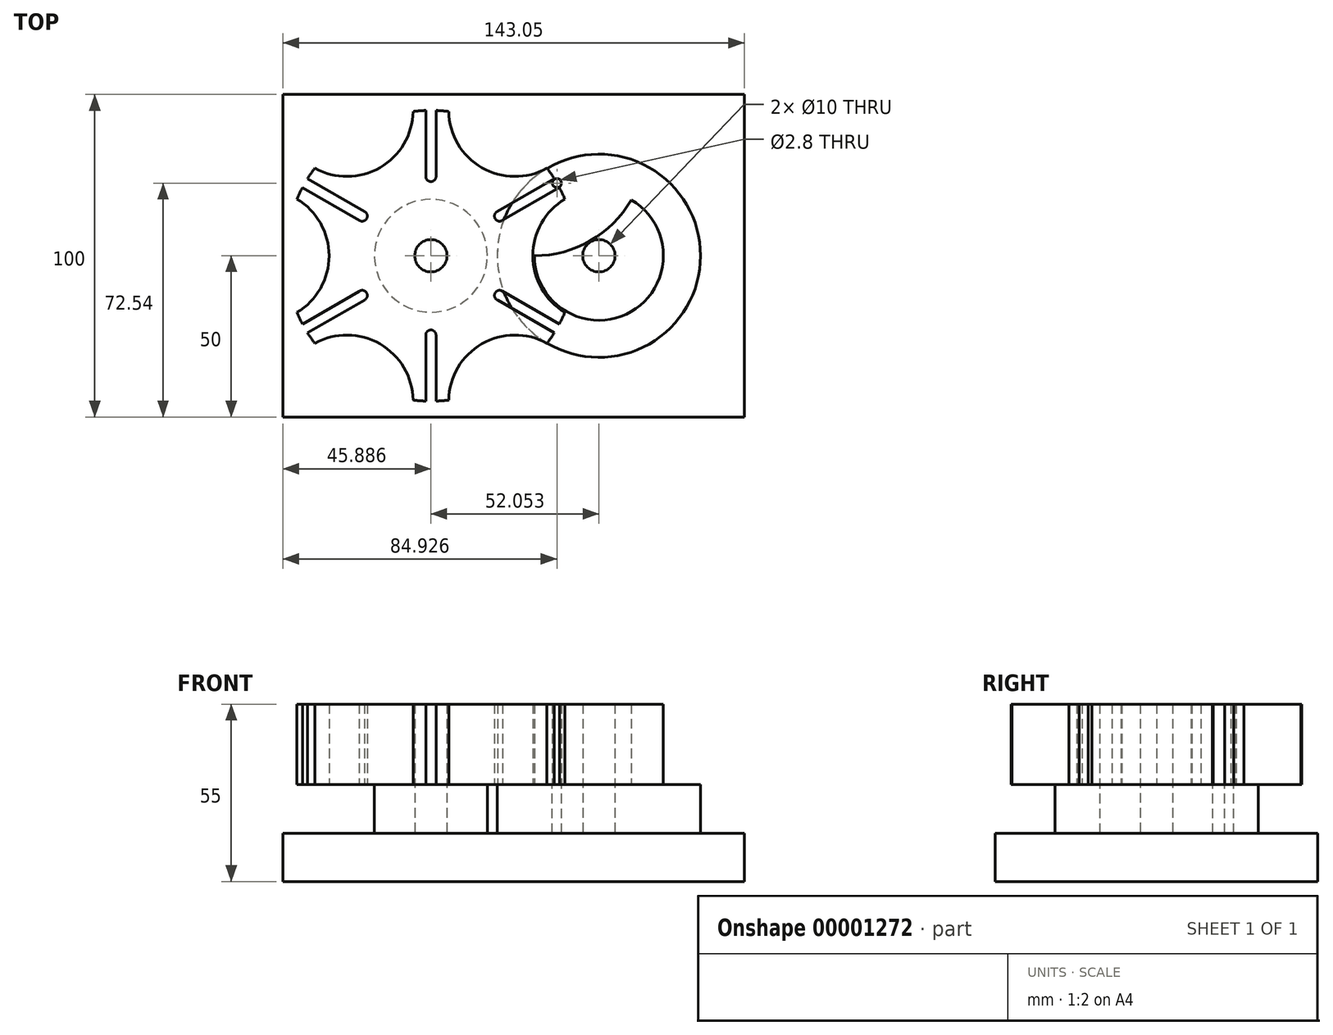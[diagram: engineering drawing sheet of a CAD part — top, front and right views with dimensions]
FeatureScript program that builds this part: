
annotation { "Feature Type Name" : "Feature", "Feature Type Description" : "" }
export const myFeature = defineFeature(function(context is Context, id is Id, definition is map)
    precondition{}
    {
        {
            var Q0;
            Q0=qCreatedBy(makeId("Top.planeOp"),FACE);
            var sketch = newSketch(context, id + "F0", { "sketchPlane" : qUnion([Q0])});
            skCircle(sketch, "E0", {"center": v(-6.18, 0) * mm, "radius": 45.08 * mm});
            skCircle(sketch, "E1", {"center": v(45.87, 0) * mm, "radius": 31.5 * mm});
            skCircle(sketch, "E2", {"center": v(45.87, 0) * mm, "radius": 20 * mm});
            skLineSegment(sketch, "E3", {"start": v(-6.18, 0) * mm, "end": v(-6.18, 45.08) * mm, "construction": true});
            skLineSegment(sketch, "E4", {"start": v(45.87, 0) * mm, "end": v(45.87, 31.5) * mm, "construction": true});
            skLineSegment(sketch, "E5", {"start": v(45.87, 20) * mm, "end": v(45.87, 31.5) * mm, "construction": true});
            skLineSegment(sketch, "E6", {"start": v(-6.18, 0) * mm, "end": v(45.87, 0) * mm, "construction": true});
            skLineSegment(sketch, "E7", {"start": v(45.87, 0) * mm, "end": v(32.86, 22.54) * mm, "construction": true});
            skLineSegment(sketch, "E8", {"start": v(32.86, 22.54) * mm, "end": v(-6.18, 0) * mm, "construction": true});
            skCircle(sketch, "E9", {"center": v(45.87, 0) * mm, "radius": 26.03 * mm, "construction": true});
            skLineSegment(sketch, "E10", {"start": v(32.86, 22.54) * mm, "end": v(15.21, 53.1) * mm, "construction": true});
            skLineSegment(sketch, "E11", {"start": v(32.86, 22.54) * mm, "end": v(15.11, 12.3) * mm});
            skArc(sketch, "E12", {"start": v(14.32, 13.67) * mm, "mid": v(13.77, 11.44) * mm, "end": v(16.03, 11) * mm});
            skLineSegment(sketch, "E13", {"start": v(16.03, 11) * mm, "end": v(33.65, 21.17) * mm});
            skLineSegment(sketch, "E14", {"start": v(32.04, 23.9) * mm, "end": v(14.32, 13.67) * mm});
            skCircle(sketch, "E15", {"center": v(32.86, 22.54) * mm, "radius": 1.4 * mm});
            skArc(sketch, "E16", {"start": v(35.62, 17.75) * mm, "mid": v(25.37, 0.17) * mm, "end": v(35.33, -17.58) * mm});
            skLineSegment(sketch, "E17.1.0", {"start": v(-7.77, 45.05) * mm, "end": v(-7.77, 24.59) * mm});
            skArc(sketch, "E17.1.1", {"start": v(-7.77, 24.59) * mm, "mid": v(-6.11, 23) * mm, "end": v(-4.6, 24.73) * mm});
            skArc(sketch, "E17.1.2", {"start": v(-0.65, 44.74) * mm, "mid": v(9.6, 27.33) * mm, "end": v(29.8, 27.16) * mm});
            skLineSegment(sketch, "E17.1.3", {"start": v(-4.6, 24.73) * mm, "end": v(-4.6, 45.08) * mm});
            skLineSegment(sketch, "E17.2.0", {"start": v(-46, 21.15) * mm, "end": v(-28.27, 10.92) * mm});
            skArc(sketch, "E17.2.1", {"start": v(-28.27, 10.92) * mm, "mid": v(-26.07, 11.56) * mm, "end": v(-26.81, 13.74) * mm});
            skArc(sketch, "E17.2.2", {"start": v(-42.46, 27.33) * mm, "mid": v(-22.1, 27.24) * mm, "end": v(-11.71, 44.74) * mm});
            skLineSegment(sketch, "E17.2.3", {"start": v(-26.81, 13.74) * mm, "end": v(-44.43, 23.91) * mm});
            skLineSegment(sketch, "E17.3.0", {"start": v(-44.4, -23.9) * mm, "end": v(-26.68, -13.67) * mm});
            skArc(sketch, "E17.3.1", {"start": v(-26.68, -13.67) * mm, "mid": v(-26.14, -11.44) * mm, "end": v(-28.4, -11) * mm});
            skArc(sketch, "E17.3.2", {"start": v(-47.99, -17.75) * mm, "mid": v(-37.74, -0.17) * mm, "end": v(-47.7, 17.58) * mm});
            skLineSegment(sketch, "E17.3.3", {"start": v(-28.4, -11) * mm, "end": v(-46.02, -21.17) * mm});
            skLineSegment(sketch, "E17.4.0", {"start": v(-4.6, -45.05) * mm, "end": v(-4.6, -24.59) * mm});
            skArc(sketch, "E17.4.1", {"start": v(-4.6, -24.59) * mm, "mid": v(-6.26, -23) * mm, "end": v(-7.77, -24.73) * mm});
            skArc(sketch, "E17.4.2", {"start": v(-11.71, -45.08) * mm, "mid": v(-21.81, -27.41) * mm, "end": v(-42.16, -27.16) * mm});
            skLineSegment(sketch, "E17.4.3", {"start": v(-7.77, -24.73) * mm, "end": v(-7.77, -45.08) * mm});
            skLineSegment(sketch, "E17.5.0", {"start": v(33.63, -21.15) * mm, "end": v(15.9, -10.92) * mm});
            skArc(sketch, "E17.5.1", {"start": v(15.9, -10.92) * mm, "mid": v(13.7, -11.56) * mm, "end": v(14.44, -13.74) * mm});
            skArc(sketch, "E17.5.2", {"start": v(30.1, -27.33) * mm, "mid": v(9.74, -27.24) * mm, "end": v(-0.65, -44.74) * mm});
            skLineSegment(sketch, "E17.5.3", {"start": v(14.44, -13.74) * mm, "end": v(32.06, -23.91) * mm});
            skCircle(sketch, "E18", {"center": v(-6.18, 0) * mm, "radius": 5 * mm});
            skLineSegment(sketch, "E19", {"start": v(25.87, 0) * mm, "end": v(25.87, 50.1) * mm, "construction": true});
            skPoint(sketch, "E20.orphan", {"position": v(-0.66, 45.08) * mm});
            skArc(sketch, "E21.trimOffspring", {"start": v(25.37, 0) * mm, "mid": v(42.97, 4.52) * mm, "end": v(55.87, 17.32) * mm});
            skCircle(sketch, "E22", {"center": v(-6.18, 0) * mm, "radius": 17.5 * mm});
            skCircle(sketch, "E23", {"center": v(45.87, 0) * mm, "radius": 5 * mm});
            skSolve(sketch);
        }
        {
            var Q0;
            {var subQ9=sQuery(id+"F0.wireOp",EDGE,"E17.1.0");Q0=makeQuery(id+"F0.imprint","IMPRINT",FACE,{"disambiguationData":[TD([[makeQuery(id+"F0.imprint","IMPRINT",EDGE,{"derivedFrom":subQ9}),-1.0]])]});}
            var Q1;
            {var subQ17=sQuery(id+"F0.wireOp",EDGE,"E12");Q1=makeQuery(id+"F0.imprint","IMPRINT",FACE,{"disambiguationData":[TD([[makeQuery(id+"F0.imprint","IMPRINT",EDGE,{"derivedFrom":subQ17}),-1.0]])]});}
            var Q2;
            {var subQ1=sQuery(id+"F0.wireOp",EDGE,"E1");var subQ3=sQuery(id+"F0.wireOp",EDGE,"E0");var subQ5=makeQuery(id+"F0.imprint","INTERSECT",VERTEX,{"disambiguationData":[OD(1.0)],"derivedFrom":[subQ3,subQ1]});Q2=makeQuery(id+"F0.imprint","IMPRINT",FACE,{"disambiguationData":[TD([[makeQuery(id+"F0.imprint","IMPRINT",EDGE,{"disambiguationData":[TD([[subQ5,-1.0]])],"derivedFrom":subQ3}),1.0]])]});}
            var Q3;
            {var subQ3=sQuery(id+"F0.wireOp",EDGE,"E0");var subQ5=sQuery(id+"F0.wireOp",EDGE,"E16");var subQ8=makeQuery(id+"F0.imprint","INTERSECT",VERTEX,{"disambiguationData":[OD(1.0)],"derivedFrom":[subQ3,subQ5]});Q3=makeQuery(id+"F0.imprint","IMPRINT",FACE,{"disambiguationData":[TD([[makeQuery(id+"F0.imprint","IMPRINT",EDGE,{"disambiguationData":[TD([[subQ8,-1.0]])],"derivedFrom":subQ3}),1.0]])]});}
            var Q4;
            {var subQ0=sQuery(id+"F0.wireOp",EDGE,"E14");var subQ3=sQuery(id+"F0.wireOp",EDGE,"E0");var subQ4=makeQuery(id+"F0.imprint","INTERSECT",VERTEX,{"derivedFrom":[subQ3,subQ0]});Q4=makeQuery(id+"F0.imprint","IMPRINT",FACE,{"disambiguationData":[TD([[makeQuery(id+"F0.imprint","IMPRINT",EDGE,{"disambiguationData":[TD([[subQ4,-1.0]])],"derivedFrom":subQ3}),1.0]])]});}
            var Q5;
            Q5=makeQuery(id+"F0.imprint","IMPRINT",FACE,{"disambiguationData":[TD([[makeQuery(id+"F0.imprint","IMPRINT",EDGE,{"derivedFrom":sQuery(id+"F0.wireOp",EDGE,"E18")}),-1.0]])]});
            extrude(context, id + "F1", {"entities" : qUnion([Q0, Q1, Q2, Q3, Q4, Q5]), "depth" : 25 * mm});
        }
        {
            var Q0;
            {var subQ0=sQuery(id+"F0.wireOp",EDGE,"E21.trimOffspring");var subQ3=sQuery(id+"F0.wireOp",EDGE,"E0");var subQ4=makeQuery(id+"F0.imprint","INTERSECT",VERTEX,{"derivedFrom":[subQ3,subQ0]});Q0=makeQuery(id+"F0.imprint","IMPRINT",FACE,{"disambiguationData":[TD([[makeQuery(id+"F0.imprint","IMPRINT",EDGE,{"disambiguationData":[TD([[subQ4,1.0]])],"derivedFrom":subQ3}),1.0]])]});}
            var Q1;
            Q1=makeQuery(id+"F0.imprint","IMPRINT",FACE,{"disambiguationData":[TD([[makeQuery(id+"F0.imprint","IMPRINT",EDGE,{"derivedFrom":sQuery(id+"F0.wireOp",EDGE,"E23")}),-1.0]])]});
            var Q2;
            {var subQ1=sQuery(id+"F0.wireOp",EDGE,"E0");var subQ4=makeQuery(id+"F0.imprint","INTERSECT",VERTEX,{"derivedFrom":[subQ1,sQuery(id+"F0.wireOp",EDGE,"E11")]});Q2=makeQuery(id+"F0.imprint","IMPRINT",FACE,{"disambiguationData":[TD([[makeQuery(id+"F0.imprint","IMPRINT",EDGE,{"disambiguationData":[TD([[subQ4,1.0]])],"derivedFrom":subQ1}),-1.0]])]});}
            var Q3;
            {var subQ1=sQuery(id+"F0.wireOp",EDGE,"E11");var subQ3=sQuery(id+"F0.wireOp",EDGE,"E0");var subQ5=makeQuery(id+"F0.imprint","INTERSECT",VERTEX,{"derivedFrom":[subQ3,subQ1]});Q3=makeQuery(id+"F0.imprint","IMPRINT",FACE,{"disambiguationData":[TD([[makeQuery(id+"F0.imprint","IMPRINT",EDGE,{"disambiguationData":[TD([[subQ5,-1.0]])],"derivedFrom":subQ3}),1.0]])]});}
            var Q4;
            {var subQ1=sQuery(id+"F0.wireOp",EDGE,"E11");var subQ3=sQuery(id+"F0.wireOp",EDGE,"E0");var subQ5=makeQuery(id+"F0.imprint","INTERSECT",VERTEX,{"derivedFrom":[subQ3,subQ1]});Q4=makeQuery(id+"F0.imprint","IMPRINT",FACE,{"disambiguationData":[TD([[makeQuery(id+"F0.imprint","IMPRINT",EDGE,{"disambiguationData":[TD([[subQ5,1.0]])],"derivedFrom":subQ3}),1.0]])]});}
            extrude(context, id + "F2", {"entities" : qUnion([Q0, Q1, Q2, Q3, Q4]), "depth" : 25 * mm});
        }
        {
            var Q0;
            {var subQ1=sQuery(id+"F0.wireOp",EDGE,"E0");var subQ11=sQuery(id+"F0.wireOp",EDGE,"E16");var subQ17=makeQuery(id+"F0.imprint","INTERSECT",VERTEX,{"disambiguationData":[OD(1.0)],"derivedFrom":[subQ1,subQ11]});Q0=makeQuery(id+"F0.imprint","IMPRINT",FACE,{"disambiguationData":[TD([[makeQuery(id+"F0.imprint","IMPRINT",EDGE,{"disambiguationData":[TD([[subQ17,1.0]])],"derivedFrom":subQ1}),-1.0]])]});}
            var Q1;
            {var subQ3=sQuery(id+"F0.wireOp",EDGE,"E0");var subQ5=sQuery(id+"F0.wireOp",EDGE,"E16");var subQ8=makeQuery(id+"F0.imprint","INTERSECT",VERTEX,{"disambiguationData":[OD(1.0)],"derivedFrom":[subQ3,subQ5]});Q1=makeQuery(id+"F0.imprint","IMPRINT",FACE,{"disambiguationData":[TD([[makeQuery(id+"F0.imprint","IMPRINT",EDGE,{"disambiguationData":[TD([[subQ8,-1.0]])],"derivedFrom":subQ3}),1.0]])]});}
            var Q2;
            {var subQ1=sQuery(id+"F0.wireOp",EDGE,"E1");var subQ3=sQuery(id+"F0.wireOp",EDGE,"E0");var subQ5=makeQuery(id+"F0.imprint","INTERSECT",VERTEX,{"disambiguationData":[OD(1.0)],"derivedFrom":[subQ3,subQ1]});Q2=makeQuery(id+"F0.imprint","IMPRINT",FACE,{"disambiguationData":[TD([[makeQuery(id+"F0.imprint","IMPRINT",EDGE,{"disambiguationData":[TD([[subQ5,-1.0]])],"derivedFrom":subQ3}),1.0]])]});}
            var Q3;
            {var subQ0=sQuery(id+"F0.wireOp",EDGE,"E17.5.0");var subQ3=sQuery(id+"F0.wireOp",EDGE,"E0");var subQ4=makeQuery(id+"F0.imprint","INTERSECT",VERTEX,{"derivedFrom":[subQ3,subQ0]});Q3=makeQuery(id+"F0.imprint","IMPRINT",FACE,{"disambiguationData":[TD([[makeQuery(id+"F0.imprint","IMPRINT",EDGE,{"disambiguationData":[TD([[subQ4,1.0]])],"derivedFrom":subQ3}),1.0]])]});}
            var Q4;
            {var subQ0=sQuery(id+"F0.wireOp",EDGE,"E13");var subQ3=sQuery(id+"F0.wireOp",EDGE,"E0");var subQ4=makeQuery(id+"F0.imprint","INTERSECT",VERTEX,{"derivedFrom":[subQ3,subQ0]});Q4=makeQuery(id+"F0.imprint","IMPRINT",FACE,{"disambiguationData":[TD([[makeQuery(id+"F0.imprint","IMPRINT",EDGE,{"disambiguationData":[TD([[subQ4,-1.0]])],"derivedFrom":subQ3}),1.0]])]});}
            var Q5;
            {var subQ3=sQuery(id+"F0.wireOp",EDGE,"E0");var subQ5=sQuery(id+"F0.wireOp",EDGE,"E14");var subQ8=makeQuery(id+"F0.imprint","INTERSECT",VERTEX,{"derivedFrom":[subQ3,subQ5]});Q5=makeQuery(id+"F0.imprint","IMPRINT",FACE,{"disambiguationData":[TD([[makeQuery(id+"F0.imprint","IMPRINT",EDGE,{"disambiguationData":[TD([[subQ8,1.0]])],"derivedFrom":subQ3}),1.0]])]});}
            var Q6;
            {var subQ0=sQuery(id+"F0.wireOp",EDGE,"E14");var subQ3=sQuery(id+"F0.wireOp",EDGE,"E0");var subQ4=makeQuery(id+"F0.imprint","INTERSECT",VERTEX,{"derivedFrom":[subQ3,subQ0]});Q6=makeQuery(id+"F0.imprint","IMPRINT",FACE,{"disambiguationData":[TD([[makeQuery(id+"F0.imprint","IMPRINT",EDGE,{"disambiguationData":[TD([[subQ4,-1.0]])],"derivedFrom":subQ3}),1.0]])]});}
            var Q7;
            Q7=makeQuery(id+"F0.imprint","IMPRINT",FACE,{"disambiguationData":[TD([[makeQuery(id+"F0.imprint","IMPRINT",EDGE,{"derivedFrom":sQuery(id+"F0.wireOp",EDGE,"E23")}),-1.0]])]});
            var Q8;
            {var subQ0=sQuery(id+"F0.wireOp",EDGE,"E21.trimOffspring");var subQ3=sQuery(id+"F0.wireOp",EDGE,"E0");var subQ4=makeQuery(id+"F0.imprint","INTERSECT",VERTEX,{"derivedFrom":[subQ3,subQ0]});Q8=makeQuery(id+"F0.imprint","IMPRINT",FACE,{"disambiguationData":[TD([[makeQuery(id+"F0.imprint","IMPRINT",EDGE,{"disambiguationData":[TD([[subQ4,1.0]])],"derivedFrom":subQ3}),1.0]])]});}
            var Q9;
            {var subQ1=sQuery(id+"F0.wireOp",EDGE,"E0");var subQ3=sQuery(id+"F0.wireOp",EDGE,"E2");var subQ5=makeQuery(id+"F0.imprint","INTERSECT",VERTEX,{"disambiguationData":[OD(0.0)],"derivedFrom":[subQ1,subQ3]});Q9=makeQuery(id+"F0.imprint","IMPRINT",FACE,{"disambiguationData":[TD([[makeQuery(id+"F0.imprint","IMPRINT",EDGE,{"disambiguationData":[TD([[subQ5,1.0]])],"derivedFrom":subQ1}),-1.0]])]});}
            var Q10;
            {var subQ1=sQuery(id+"F0.wireOp",EDGE,"E2");var subQ3=sQuery(id+"F0.wireOp",EDGE,"E0");var subQ5=makeQuery(id+"F0.imprint","INTERSECT",VERTEX,{"disambiguationData":[OD(0.0)],"derivedFrom":[subQ3,subQ1]});Q10=makeQuery(id+"F0.imprint","IMPRINT",FACE,{"disambiguationData":[TD([[makeQuery(id+"F0.imprint","IMPRINT",EDGE,{"disambiguationData":[TD([[subQ5,1.0]])],"derivedFrom":subQ3}),1.0]])]});}
            var Q11;
            {var subQ3=sQuery(id+"F0.wireOp",EDGE,"E16");var subQ5=sQuery(id+"F0.wireOp",EDGE,"E0");var subQ6=makeQuery(id+"F0.imprint","INTERSECT",VERTEX,{"disambiguationData":[OD(1.0)],"derivedFrom":[subQ5,subQ3]});Q11=makeQuery(id+"F0.imprint","IMPRINT",FACE,{"disambiguationData":[TD([[makeQuery(id+"F0.imprint","IMPRINT",EDGE,{"disambiguationData":[TD([[subQ6,1.0]])],"derivedFrom":subQ5}),1.0]])]});}
            var Q12;
            {var subQ0=sQuery(id+"F0.wireOp",EDGE,"E16");var subQ3=sQuery(id+"F0.wireOp",EDGE,"E0");var subQ4=makeQuery(id+"F0.imprint","INTERSECT",VERTEX,{"disambiguationData":[OD(0.0)],"derivedFrom":[subQ3,subQ0]});Q12=makeQuery(id+"F0.imprint","IMPRINT",FACE,{"disambiguationData":[TD([[makeQuery(id+"F0.imprint","IMPRINT",EDGE,{"disambiguationData":[TD([[subQ4,-1.0]])],"derivedFrom":subQ3}),1.0]])]});}
            extrude(context, id + "F3", {"entities" : qUnion([Q0, Q1, Q2, Q3, Q4, Q5, Q6, Q7, Q8, Q9, Q10, Q11, Q12]), "operationType" : NewBodyOperationType.ADD, "oppositeDirection" : true, "depth" : 15 * mm});
        }
        {
            var Q0;
            Q0=makeQuery(id+"F0.imprint","IMPRINT",FACE,{"disambiguationData":[TD([[makeQuery(id+"F0.imprint","IMPRINT",EDGE,{"derivedFrom":sQuery(id+"F0.wireOp",EDGE,"E18")}),-1.0]])]});
            extrude(context, id + "F4", {"entities" : qUnion([Q0]), "operationType" : NewBodyOperationType.ADD, "oppositeDirection" : true, "depth" : 15 * mm});
        }
        {
            var Q0;
            Q0=makeQuery(id+"F3.opExtrude","CAP_FACE",FACE,{"disambiguationData":[OSD([sQuery(id+"F0.wireOp",EDGE,"E1"),sQuery(id+"F0.wireOp",EDGE,"E15"),sQuery(id+"F0.wireOp",EDGE,"E23")])],"isStart":false});
            var sketch = newSketch(context, id + "F5", { "sketchPlane" : qUnion([Q0])});
            skLineSegment(sketch, "E24.bottom", {"start": v(90.98, 50) * mm, "end": v(-52.07, 50) * mm});
            skLineSegment(sketch, "E24.top", {"start": v(90.98, -50) * mm, "end": v(-52.07, -50) * mm});
            skLineSegment(sketch, "E24.left", {"start": v(90.98, 50) * mm, "end": v(90.98, -50) * mm});
            skLineSegment(sketch, "E24.right", {"start": v(-52.07, 50) * mm, "end": v(-52.07, -50) * mm});
            skCircle(sketch, "E25", {"center": v(45.87, 0) * mm, "radius": 5 * mm});
            skSolve(sketch);
        }
        {
            var Q0;
            Q0=makeQuery(id+"F5.imprint","IMPRINT",FACE,{"disambiguationData":[TD([[makeQuery(id+"F5.imprint","IMPRINT",EDGE,{"derivedFrom":sQuery(id+"F5.wireOp",EDGE,"E24.bottom")}),1.0]])]});
            var Q1;
            Q1=makeQuery(id+"F5.imprint","IMPRINT",FACE,{"disambiguationData":[TD([[makeQuery(id+"F5.imprint","IMPRINT",EDGE,{"derivedFrom":sQuery(id+"F5.wireOp",EDGE,"E25")}),1.0]])]});
            var Q2;
            Q2=makeQuery(id+"F5.imprint","IMPRINT",FACE,{"disambiguationData":[TD([[makeQuery(id+"F5.imprint","IMPRINT",EDGE,{"derivedFrom":makeQuery(id+"F3.opExtrude","CAP_EDGE",EDGE,{"disambiguationData":[OSD([sQuery(id+"F0.wireOp",EDGE,"E15")])],"isStart":false})}),-1.0]])]});
            var Q3;
            Q3=makeQuery(id+"F5.imprint","IMPRINT",FACE,{"disambiguationData":[TD([[makeQuery(id+"F5.imprint","IMPRINT",EDGE,{"derivedFrom":sQuery(id+"F5.wireOp",EDGE,"E25")}),-1.0]])]});
            extrude(context, id + "F6", {"entities" : qUnion([Q0, Q1, Q2, Q3]), "depth" : 15 * mm});
        }
    });
